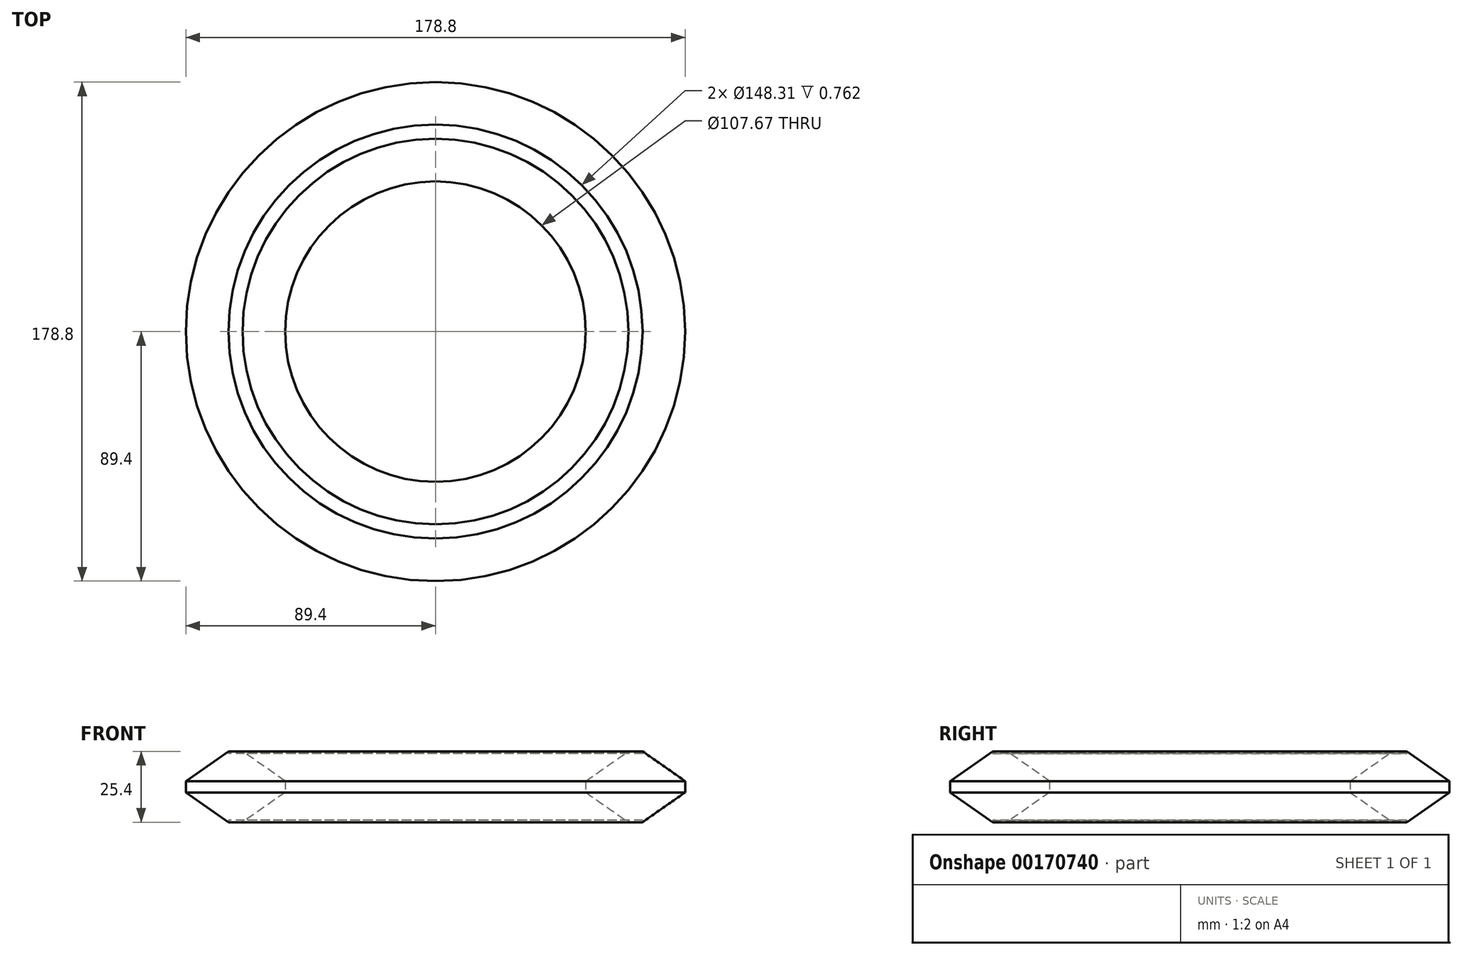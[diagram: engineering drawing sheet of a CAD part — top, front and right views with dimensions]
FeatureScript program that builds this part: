
annotation { "Feature Type Name" : "Feature", "Feature Type Description" : "" }
export const myFeature = defineFeature(function(context is Context, id is Id, definition is map)
    precondition{}
    {
        {
            var Q0;
            Q0=qCreatedBy(makeId("Top.planeOp"),FACE);
            var sketch = newSketch(context, id + "F0", { "sketchPlane" : qUnion([Q0])});
            skCircle(sketch, "E0", {"center": v(0, 0) * mm, "radius": 89.4 * mm});
            skCircle(sketch, "E1.0", {"center": v(0, 0) * mm, "radius": 53.84 * mm});
            skSolve(sketch);
        }
        {
            var Q0;
            Q0=makeQuery(id+"F0.imprint","IMPRINT",FACE,{"disambiguationData":[TD([[makeQuery(id+"F0.imprint","IMPRINT",EDGE,{"derivedFrom":sQuery(id+"F0.wireOp",EDGE,"E0")}),1.0]])]});
            extrude(context, id + "F1", {"entities" : qUnion([Q0]), "depth" : 25.4 * mm});
        }
        {
            var Q0;
            Q0=makeQuery(id+"F1.opExtrude","CAP_EDGE",EDGE,{"disambiguationData":[OSD([sQuery(id+"F0.wireOp",EDGE,"E0")])],"isStart":false});
            var Q1;
            Q1=makeQuery(id+"F1.opExtrude","CAP_EDGE",EDGE,{"disambiguationData":[OSD([sQuery(id+"F0.wireOp",EDGE,"E0")])],"isStart":true});
            var Q2;
            Q2=makeQuery(id+"F1.opExtrude","CAP_EDGE",EDGE,{"disambiguationData":[OSD([sQuery(id+"F0.wireOp",EDGE,"E1.0")])],"isStart":false});
            var Q3;
            Q3=makeQuery(id+"F1.opExtrude","CAP_EDGE",EDGE,{"disambiguationData":[OSD([sQuery(id+"F0.wireOp",EDGE,"E1.0")])],"isStart":true});
            chamfer(context, id + "F2", {"entities" : qUnion([Q0, Q1, Q2, Q3]), "chamferType" : ChamferType.OFFSET_ANGLE, "width" : 15.24 * mm, "oppositeDirection" : false, "angle" : 35 * degree, "tangentPropagation" : true});
        }
        {
            var Q0;
            Q0=makeQuery(id+"F1.opExtrude","CAP_FACE",FACE,{"disambiguationData":[OSD([sQuery(id+"F0.wireOp",EDGE,"E0"),sQuery(id+"F0.wireOp",EDGE,"E1.0")])],"isStart":false});
            var Q1;
            Q1=makeQuery(id+"F1.opExtrude","CAP_FACE",FACE,{"disambiguationData":[OSD([sQuery(id+"F0.wireOp",EDGE,"E0"),sQuery(id+"F0.wireOp",EDGE,"E1.0")])],"isStart":true});
            extrude(context, id + "F3", {"entities" : qUnion([Q0, Q1]), "operationType" : NewBodyOperationType.REMOVE, "oppositeDirection" : true, "depth" : 0.76 * mm});
        }
        {
            var Q0;
            Q0=makeQuery(id+"F1.opExtrude","CAP_FACE",FACE,{"disambiguationData":[OSD([sQuery(id+"F0.wireOp",EDGE,"E0"),sQuery(id+"F0.wireOp",EDGE,"E1.0")])],"isStart":true});
            extrude(context, id + "F4", {"entities" : qUnion([Q0]), "operationType" : NewBodyOperationType.REMOVE, "oppositeDirection" : true, "depth" : 0.76 * mm});
        }
    });
